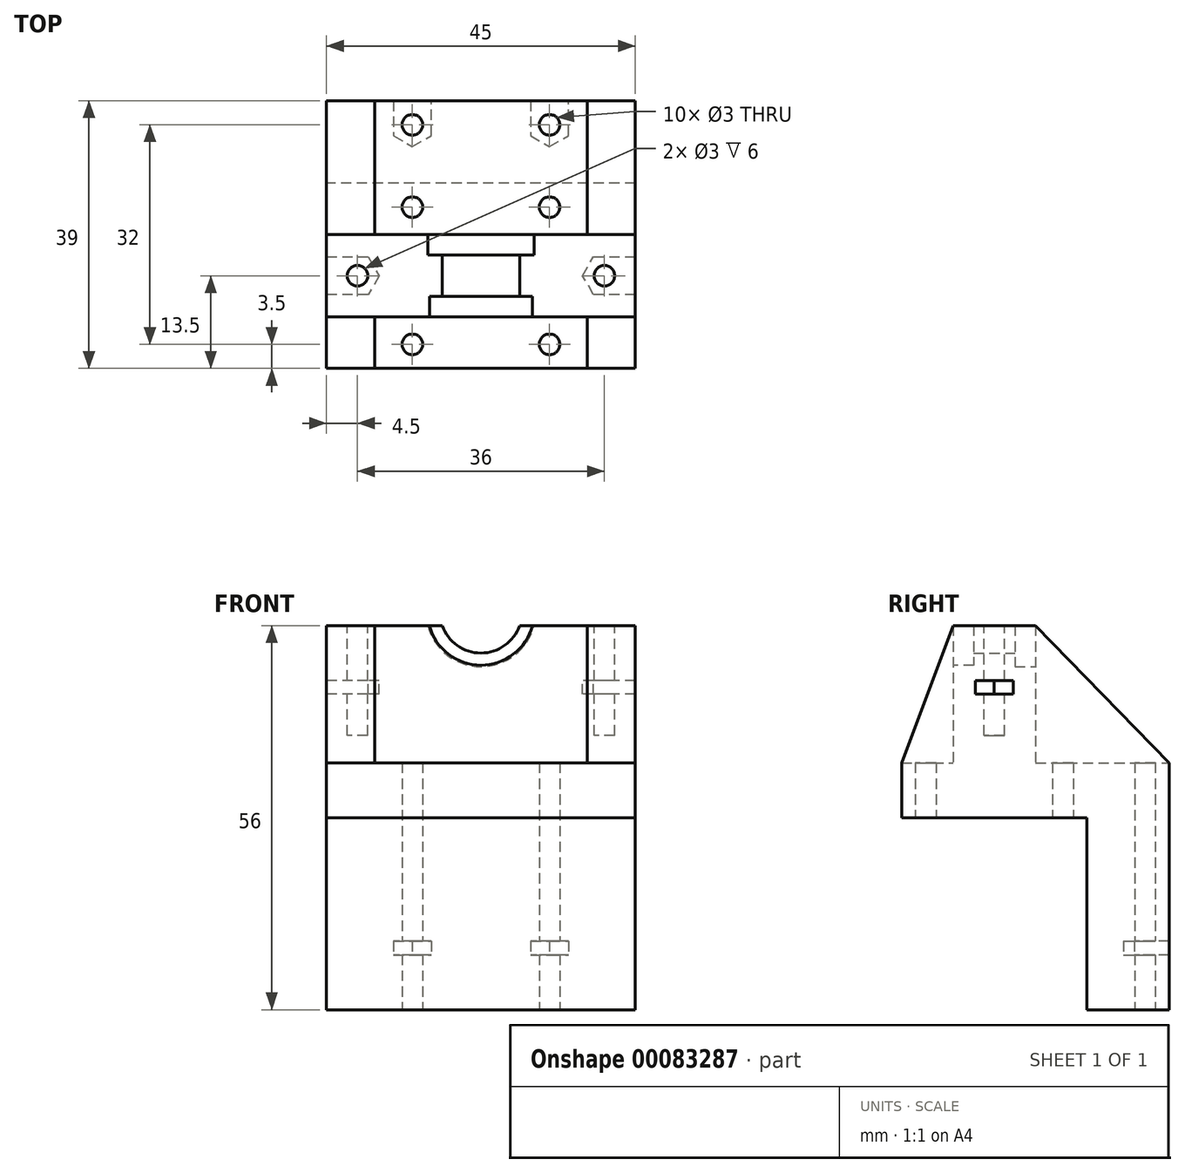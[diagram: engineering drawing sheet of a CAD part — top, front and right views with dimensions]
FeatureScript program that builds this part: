
annotation { "Feature Type Name" : "Feature", "Feature Type Description" : "" }
export const myFeature = defineFeature(function(context is Context, id is Id, definition is map)
    precondition{}
    {
        {
            var Q0;
            Q0=qCreatedBy(makeId("Top.planeOp"),FACE);
            var sketch = newSketch(context, id + "F0", { "sketchPlane" : qUnion([Q0])});
            skLineSegment(sketch, "E0.bottom", {"start": v(22.5, 13.5) * mm, "end": v(-22.5, 13.5) * mm});
            skLineSegment(sketch, "E0.top", {"start": v(22.5, -13.5) * mm, "end": v(-22.5, -13.5) * mm});
            skLineSegment(sketch, "E0.left", {"start": v(22.5, 13.5) * mm, "end": v(22.5, -13.5) * mm});
            skLineSegment(sketch, "E0.right", {"start": v(-22.5, 13.5) * mm, "end": v(-22.5, -13.5) * mm});
            skPoint(sketch, "E0.middle", {"position": v(0, 0) * mm});
            skLineSegment(sketch, "E1.bottom", {"start": v(10, 10) * mm, "end": v(-10, 10) * mm, "construction": true});
            skLineSegment(sketch, "E1.top", {"start": v(10, -10) * mm, "end": v(-10, -10) * mm, "construction": true});
            skLineSegment(sketch, "E1.left", {"start": v(10, 10) * mm, "end": v(10, -10) * mm, "construction": true});
            skLineSegment(sketch, "E1.right", {"start": v(-10, 10) * mm, "end": v(-10, -10) * mm, "construction": true});
            skCircle(sketch, "E2", {"center": v(10, 10) * mm, "radius": 1.5 * mm});
            skCircle(sketch, "E3", {"center": v(10, -10) * mm, "radius": 1.5 * mm});
            skCircle(sketch, "E4", {"center": v(-10, -10) * mm, "radius": 1.5 * mm});
            skCircle(sketch, "E5", {"center": v(-10, 10) * mm, "radius": 1.5 * mm});
            skLineSegment(sketch, "E6.top", {"start": v(22.5, 25.5) * mm, "end": v(-22.5, 25.5) * mm});
            skLineSegment(sketch, "E6.left", {"start": v(22.5, 13.5) * mm, "end": v(22.5, 25.5) * mm});
            skLineSegment(sketch, "E6.right", {"start": v(-22.5, 13.5) * mm, "end": v(-22.5, 25.5) * mm});
            skCircle(sketch, "E7", {"center": v(-10, 22) * mm, "radius": 1.5 * mm});
            skCircle(sketch, "E8", {"center": v(10, 22) * mm, "radius": 1.5 * mm});
            skSolve(sketch);
        }
        {
            var Q0;
            Q0=makeQuery(id+"F0.imprint","IMPRINT",FACE,{"disambiguationData":[TD([[makeQuery(id+"F0.imprint","IMPRINT",EDGE,{"derivedFrom":sQuery(id+"F0.wireOp",EDGE,"E0.top")}),-1.0]])]});
            var Q1;
            Q1=makeQuery(id+"F0.imprint","IMPRINT",FACE,{"disambiguationData":[TD([[makeQuery(id+"F0.imprint","IMPRINT",EDGE,{"derivedFrom":sQuery(id+"F0.wireOp",EDGE,"E0.bottom")}),-1.0]])]});
            extrude(context, id + "F1", {"entities" : qUnion([Q0, Q1]), "depth" : 8 * mm});
        }
        {
            var Q0;
            Q0=makeQuery(id+"F0.imprint","IMPRINT",FACE,{"disambiguationData":[TD([[makeQuery(id+"F0.imprint","IMPRINT",EDGE,{"derivedFrom":sQuery(id+"F0.wireOp",EDGE,"E0.bottom")}),-1.0]])]});
            extrude(context, id + "F2", {"entities" : qUnion([Q0]), "operationType" : NewBodyOperationType.ADD, "oppositeDirection" : true, "depth" : 28 * mm});
        }
        {
            var Q0;
            Q0=makeQuery(id+"F2.opExtrude","CAP_FACE",FACE,{"disambiguationData":[OSD([sQuery(id+"F0.wireOp",EDGE,"E0.bottom"),sQuery(id+"F0.wireOp",EDGE,"E6.top"),sQuery(id+"F0.wireOp",EDGE,"E6.left"),sQuery(id+"F0.wireOp",EDGE,"E6.right"),sQuery(id+"F0.wireOp",EDGE,"E7"),sQuery(id+"F0.wireOp",EDGE,"E8")])],"isStart":false});
            var sketch = newSketch(context, id + "F3", { "sketchPlane" : qUnion([Q0])});
            skCircle(sketch, "E9.cCircle", {"center": v(-10, -22) * mm, "radius": 2.75 * mm, "construction": true});
            skLineSegment(sketch, "E9.0", {"start": v(-10, -18.82) * mm, "end": v(-7.25, -20.41) * mm});
            skLineSegment(sketch, "E9.1", {"start": v(-7.25, -20.41) * mm, "end": v(-7.25, -23.59) * mm});
            skLineSegment(sketch, "E9.4", {"start": v(-12.75, -23.59) * mm, "end": v(-12.75, -20.41) * mm});
            skLineSegment(sketch, "E9.5", {"start": v(-12.75, -20.41) * mm, "end": v(-10, -18.82) * mm});
            skPoint(sketch, "E9.0.midPoint", {"position": v(-8.63, -19.62) * mm});
            skCircle(sketch, "E10.cCircle", {"center": v(10, -22) * mm, "radius": 2.75 * mm, "construction": true});
            skLineSegment(sketch, "E10.2", {"start": v(7.25, -23.59) * mm, "end": v(7.25, -20.41) * mm});
            skLineSegment(sketch, "E10.3", {"start": v(7.25, -20.41) * mm, "end": v(10, -18.82) * mm});
            skLineSegment(sketch, "E10.4", {"start": v(10, -18.82) * mm, "end": v(12.75, -20.41) * mm});
            skLineSegment(sketch, "E10.5", {"start": v(12.75, -20.41) * mm, "end": v(12.75, -23.59) * mm});
            skPoint(sketch, "E10.0.midPoint", {"position": v(11.37, -24.38) * mm});
            skLineSegment(sketch, "E11", {"start": v(-7.25, -23.59) * mm, "end": v(-7.25, -25.5) * mm});
            skLineSegment(sketch, "E12", {"start": v(-12.75, -23.59) * mm, "end": v(-12.75, -25.5) * mm});
            skLineSegment(sketch, "E13", {"start": v(7.25, -23.59) * mm, "end": v(7.25, -25.5) * mm});
            skLineSegment(sketch, "E14", {"start": v(12.75, -23.59) * mm, "end": v(12.75, -25.5) * mm});
            skSolve(sketch);
        }
        {
            var Q0;
            Q0=makeQuery(id+"F3.imprint","IMPRINT",FACE,{"disambiguationData":[TD([[makeQuery(id+"F3.imprint","IMPRINT",EDGE,{"derivedFrom":sQuery(id+"F3.wireOp",EDGE,"E9.0")}),-1.0]])]});
            var Q1;
            Q1=makeQuery(id+"F3.imprint","IMPRINT",FACE,{"disambiguationData":[TD([[makeQuery(id+"F3.imprint","IMPRINT",EDGE,{"derivedFrom":sQuery(id+"F3.wireOp",EDGE,"E10.2")}),-1.0]])]});
            extrude(context, id + "F4", {"entities" : qUnion([Q0, Q1]), "operationType" : NewBodyOperationType.REMOVE, "oppositeDirection" : true, "depth" : 10 * mm});
        }
        {
            var Q0;
            Q0=makeQuery(id+"F3.imprint","IMPRINT",FACE,{"disambiguationData":[TD([[makeQuery(id+"F3.imprint","IMPRINT",EDGE,{"derivedFrom":sQuery(id+"F3.wireOp",EDGE,"E10.2")}),-1.0]])]});
            var Q1;
            Q1=makeQuery(id+"F3.imprint","IMPRINT",FACE,{"disambiguationData":[TD([[makeQuery(id+"F3.imprint","IMPRINT",EDGE,{"derivedFrom":sQuery(id+"F3.wireOp",EDGE,"E9.0")}),-1.0]])]});
            extrude(context, id + "F5", {"entities" : qUnion([Q0, Q1]), "operationType" : NewBodyOperationType.ADD, "oppositeDirection" : true, "depth" : 8 * mm});
        }
        {
            var Q0;
            Q0=makeQuery(id+"F1.opExtrude","CAP_FACE",FACE,{"disambiguationData":[OSD([sQuery(id+"F0.wireOp",EDGE,"E0.top"),sQuery(id+"F0.wireOp",EDGE,"E0.left"),sQuery(id+"F0.wireOp",EDGE,"E0.right"),sQuery(id+"F0.wireOp",EDGE,"E2"),sQuery(id+"F0.wireOp",EDGE,"E3"),sQuery(id+"F0.wireOp",EDGE,"E4"),sQuery(id+"F0.wireOp",EDGE,"E5"),sQuery(id+"F0.wireOp",EDGE,"E6.top"),sQuery(id+"F0.wireOp",EDGE,"E6.left"),sQuery(id+"F0.wireOp",EDGE,"E6.right"),sQuery(id+"F0.wireOp",EDGE,"E7"),sQuery(id+"F0.wireOp",EDGE,"E8")])],"isStart":false});
            var sketch = newSketch(context, id + "F6", { "sketchPlane" : qUnion([Q0])});
            skLineSegment(sketch, "E15.bottom", {"start": v(-22.5, -13.5) * mm, "end": v(-15.5, -13.5) * mm});
            skLineSegment(sketch, "E15.top", {"start": v(-22.5, 25.5) * mm, "end": v(-15.5, 25.5) * mm});
            skLineSegment(sketch, "E15.left", {"start": v(-22.5, -13.5) * mm, "end": v(-22.5, 25.5) * mm});
            skLineSegment(sketch, "E15.right", {"start": v(-15.5, -13.5) * mm, "end": v(-15.5, 25.5) * mm});
            skLineSegment(sketch, "E16.bottom", {"start": v(22.5, -13.5) * mm, "end": v(15.5, -13.5) * mm});
            skLineSegment(sketch, "E16.top", {"start": v(22.5, 25.5) * mm, "end": v(15.5, 25.5) * mm});
            skLineSegment(sketch, "E16.left", {"start": v(22.5, -13.5) * mm, "end": v(22.5, 25.5) * mm});
            skLineSegment(sketch, "E16.right", {"start": v(15.5, -13.5) * mm, "end": v(15.5, 25.5) * mm});
            skLineSegment(sketch, "E17.bottom", {"start": v(-15.5, -6) * mm, "end": v(15.5, -6) * mm});
            skLineSegment(sketch, "E17.top", {"start": v(-15.5, 6) * mm, "end": v(15.5, 6) * mm});
            skLineSegment(sketch, "E17.left", {"start": v(-15.5, -6) * mm, "end": v(-15.5, 6) * mm});
            skLineSegment(sketch, "E17.right", {"start": v(15.5, -6) * mm, "end": v(15.5, 6) * mm});
            skSolve(sketch);
        }
        {
            var Q0;
            Q0 = qSketchRegion(id + "F6", true);
            extrude(context, id + "F7", {"entities" : qUnion([Q0]), "operationType" : NewBodyOperationType.ADD, "depth" : 20 * mm});
        }
        {
            var Q0;
            Q0=makeQuery(id+"F7.opExtrude","CAP_EDGE",EDGE,{"disambiguationData":[OSD([sQuery(id+"F6.wireOp",EDGE,"E15.top")])],"isStart":false});
            var Q1;
            Q1=makeQuery(id+"F7.opExtrude","CAP_EDGE",EDGE,{"disambiguationData":[OSD([sQuery(id+"F6.wireOp",EDGE,"E16.top")])],"isStart":false});
            chamfer(context, id + "F8", {"entities" : qUnion([Q0, Q1]), "chamferType" : ChamferType.TWO_OFFSETS, "width1" : 19.5 * mm, "oppositeDirection" : false, "width2" : 20 * mm, "tangentPropagation" : true});
        }
        {
            var Q0;
            Q0=makeQuery(id+"F7.opExtrude","CAP_EDGE",EDGE,{"disambiguationData":[OSD([sQuery(id+"F6.wireOp",EDGE,"E16.bottom")])],"isStart":false});
            var Q1;
            Q1=makeQuery(id+"F7.opExtrude","CAP_EDGE",EDGE,{"disambiguationData":[OSD([sQuery(id+"F6.wireOp",EDGE,"E15.bottom")])],"isStart":false});
            chamfer(context, id + "F9", {"entities" : qUnion([Q0, Q1]), "chamferType" : ChamferType.TWO_OFFSETS, "width1" : 20 * mm, "oppositeDirection" : false, "width2" : 7.5 * mm, "tangentPropagation" : true});
        }
        {
            var Q0;
            Q0=makeQuery(id+"F7.opExtrude","SWEPT_FACE",FACE,{"disambiguationData":[OSD([sQuery(id+"F6.wireOp",EDGE,"E17.top")])]});
            var sketch = newSketch(context, id + "F10", { "sketchPlane" : qUnion([Q0])});
            skCircle(sketch, "E18", {"center": v(0, 30) * mm, "radius": 8 * mm});
            skCircle(sketch, "E19", {"center": v(0, 30) * mm, "radius": 6 * mm});
            skSolve(sketch);
        }
        {
            var Q0;
            {var subQ0=sQuery(id+"F10.wireOp",EDGE,"E19");var subQ1=makeQuery(id+"F7.opExtrude","CAP_EDGE",EDGE,{"disambiguationData":[OSD([sQuery(id+"F6.wireOp",EDGE,"E17.top")])],"isStart":false});var subQ2=makeQuery(id+"F10.imprint","INTERSECT",VERTEX,{"disambiguationData":[OD(0.0)],"derivedFrom":[subQ1,subQ0]});Q0=makeQuery(id+"F10.imprint","IMPRINT",FACE,{"disambiguationData":[TD([[makeQuery(id+"F10.imprint","IMPRINT",EDGE,{"disambiguationData":[TD([[subQ2,1.0]])],"derivedFrom":subQ0}),1.0]])]});}
            extrude(context, id + "F11", {"entities" : qUnion([Q0]), "operationType" : NewBodyOperationType.REMOVE, "endBound" : BoundingType.THROUGH_ALL, "oppositeDirection" : true, "depth" : 25 * mm});
        }
        {
            var Q0;
            {var subQ0=sQuery(id+"F10.wireOp",EDGE,"E18");var subQ1=makeQuery(id+"F7.opExtrude","CAP_EDGE",EDGE,{"disambiguationData":[OSD([sQuery(id+"F6.wireOp",EDGE,"E17.top")])],"isStart":false});var subQ2=makeQuery(id+"F10.imprint","INTERSECT",VERTEX,{"disambiguationData":[OD(0.0)],"derivedFrom":[subQ1,subQ0]});Q0=makeQuery(id+"F10.imprint","IMPRINT",FACE,{"disambiguationData":[TD([[makeQuery(id+"F10.imprint","IMPRINT",EDGE,{"disambiguationData":[TD([[subQ2,1.0]])],"derivedFrom":subQ0}),1.0]])]});}
            extrude(context, id + "F12", {"entities" : qUnion([Q0]), "operationType" : NewBodyOperationType.REMOVE, "oppositeDirection" : true, "depth" : 3 * mm});
        }
        {
            var Q0;
            Q0=makeQuery(id+"F7.opExtrude","SWEPT_FACE",FACE,{"disambiguationData":[OSD([sQuery(id+"F6.wireOp",EDGE,"E17.bottom")])]});
            var sketch = newSketch(context, id + "F13", { "sketchPlane" : qUnion([Q0])});
            skCircle(sketch, "E20", {"center": v(0, 30) * mm, "radius": 7.77 * mm});
            skSolve(sketch);
        }
        {
            var Q0;
            Q0 = qSketchRegion(id + "F13", true);
            extrude(context, id + "F14", {"entities" : qUnion([Q0]), "operationType" : NewBodyOperationType.REMOVE, "oppositeDirection" : true, "depth" : 3 * mm});
        }
        {
            var Q0;
            {var subQ0=sQuery(id+"F0.wireOp",EDGE,"E6.right");var subQ1=sQuery(id+"F6.wireOp",EDGE,"E15.right");var subQ2=sQuery(id+"F6.wireOp",EDGE,"E15.bottom");var subQ4=sQuery(id+"F6.wireOp",EDGE,"E17.bottom");var subQ5=sQuery(id+"F6.wireOp",EDGE,"E15.left");var subQ6=sQuery(id+"F6.wireOp",EDGE,"E17.top");var subQ7=sQuery(id+"F6.wireOp",EDGE,"E15.top");Q0=makeQuery(id+"F11.boolean.opBoolean","SPLIT",FACE,{"disambiguationData":[TD([makeQuery(id+"F2.opExtrude","SWEPT_FACE",FACE,{"disambiguationData":[OSD([subQ0])]})])],"derivedFrom":makeQuery(id+"F7.opExtrude","CAP_FACE",FACE,{"disambiguationData":[OSD([subQ2,subQ7,subQ5,subQ1,sQuery(id+"F6.wireOp",EDGE,"E16.bottom"),sQuery(id+"F6.wireOp",EDGE,"E16.top"),sQuery(id+"F6.wireOp",EDGE,"E16.left"),sQuery(id+"F6.wireOp",EDGE,"E16.right"),subQ4,subQ6])],"isStart":false})});}
            var sketch = newSketch(context, id + "F15", { "sketchPlane" : qUnion([Q0])});
            skCircle(sketch, "E21.cCircle", {"center": v(-18, 0) * mm, "radius": 2.75 * mm, "construction": true});
            skLineSegment(sketch, "E21.0", {"start": v(-16.41, -2.75) * mm, "end": v(-19.59, -2.75) * mm});
            skLineSegment(sketch, "E21.3", {"start": v(-19.59, 2.75) * mm, "end": v(-16.41, 2.75) * mm});
            skLineSegment(sketch, "E21.4", {"start": v(-16.41, 2.75) * mm, "end": v(-14.82, 0) * mm});
            skLineSegment(sketch, "E21.5", {"start": v(-14.82, 0) * mm, "end": v(-16.41, -2.75) * mm});
            skPoint(sketch, "E21.0.midPoint", {"position": v(-18, -2.75) * mm});
            skCircle(sketch, "E22.cCircle", {"center": v(18, 0) * mm, "radius": 2.75 * mm, "construction": true});
            skLineSegment(sketch, "E22.0", {"start": v(16.41, -2.75) * mm, "end": v(14.82, 0) * mm});
            skLineSegment(sketch, "E22.1", {"start": v(14.82, 0) * mm, "end": v(16.41, 2.75) * mm});
            skLineSegment(sketch, "E22.2", {"start": v(16.41, 2.75) * mm, "end": v(19.59, 2.75) * mm});
            skLineSegment(sketch, "E22.5", {"start": v(19.59, -2.75) * mm, "end": v(16.41, -2.75) * mm});
            skPoint(sketch, "E22.0.midPoint", {"position": v(15.62, -1.37) * mm});
            skLineSegment(sketch, "E23", {"start": v(19.59, 2.75) * mm, "end": v(22.5, 2.75) * mm});
            skLineSegment(sketch, "E24", {"start": v(19.59, -2.75) * mm, "end": v(22.5, -2.75) * mm});
            skLineSegment(sketch, "E25", {"start": v(-19.59, -2.75) * mm, "end": v(-22.5, -2.75) * mm});
            skLineSegment(sketch, "E26", {"start": v(-19.59, 2.75) * mm, "end": v(-22.5, 2.75) * mm});
            skLineSegment(sketch, "E27", {"start": v(-22.5, -2.75) * mm, "end": v(-22.5, 2.75) * mm});
            skLineSegment(sketch, "E28", {"start": v(22.5, -2.75) * mm, "end": v(22.5, 2.75) * mm});
            skSolve(sketch);
        }
        {
            var Q0;
            Q0 = qSketchRegion(id + "F15", true);
            extrude(context, id + "F16", {"entities" : qUnion([Q0]), "operationType" : NewBodyOperationType.REMOVE, "oppositeDirection" : true, "depth" : 10 * mm});
        }
        {
            var Q0;
            Q0 = qSketchRegion(id + "F15", true);
            extrude(context, id + "F17", {"entities" : qUnion([Q0]), "operationType" : NewBodyOperationType.ADD, "oppositeDirection" : true, "depth" : 8 * mm});
        }
        {
            var Q0;
            Q0=makeQuery(id+"F15.imprint","IMPRINT",FACE,{"disambiguationData":[TD([[makeQuery(id+"F15.imprint","IMPRINT",EDGE,{"derivedFrom":sQuery(id+"F15.wireOp",EDGE,"E21.0")}),1.0]])]});
            var sketch = newSketch(context, id + "F18", { "sketchPlane" : qUnion([Q0])});
            skCircle(sketch, "E29", {"center": v(-18, 0) * mm, "radius": 1.5 * mm});
            skCircle(sketch, "E30", {"center": v(18, 0) * mm, "radius": 1.5 * mm});
            skSolve(sketch);
        }
        {
            var Q0;
            Q0 = qSketchRegion(id + "F18", true);
            extrude(context, id + "F19", {"entities" : qUnion([Q0]), "operationType" : NewBodyOperationType.REMOVE, "oppositeDirection" : true, "depth" : 16 * mm});
        }
    });
